# Revit family: Drapery_Track-Lutron-Inside_Curve-Wall_Mount new final
name_source: partatom
category: Specialty Equipment
revit_build: Autodesk Revit 2017 (Build: 20160225_1515(x64)
units: mm (PartAtom-declared; Revit-internal decimal feet)

## family parameters
Cut with Voids When Loaded = Yes
Host = Face
OmniClass Number = 23.30.60.14.21
OmniClass Title = Shades
Part Type = Normal
Room Calculation Point = No
Round Connector Dimension = Use Diameter
Shared = No

## types (3) — shared parameters
Apparent Load = 0 VA
Assembly Code = E2010320
C Radius = 1' - 8"
Default Elevation = 0' - 0"
Description = Inside Curve Wall Mounted Traditional Drapery Track System
Electronic Drive Unit D105 = Yes
Electronic Drive Unit D145 = No
Electronic Drive Unit D175 = No
Electronic Drive Unit Note = Electronic Drive Unit D105 - Carries draperies up to 105 lbs
Finish = Metal - Lutron - White
Instruction Sheet Link = http://www.lutron.com
Load Classification = Motor
Manufacturer = Lutron Electronics Co., Inc
Manufacturer Fax Number = 610-282-1243
Number of Poles = 1
Power Factor = 1
Product Documentation Link = http://www.lutron.com
Product Name = Traditional Drapery Track System
Product Page URL = http://www.lutron.com
Series = Sivoia QS
URL = http://www.lutron.com
Version = 2017 - v1.0a
Voltage = 24 V
Voltage Comment = 24-36V
Warranty URL = http://www.lutron.com
Wattage = 41 W
zero-valued in all types: Cost

## per-type parameters (varying)
| type | C 2nd Drapery | Center Draw | Constraints | Not Tandem | Single Side Draw | Tandem Draw |
| Inside Curve Wall Mounted - Left or Right Side Draw | No | No | 1 | Yes | Yes | No |
| Inside Curve Wall Mounted - Center Draw | Yes | Yes | 2 | Yes | No | No |
| Inside Curve Wall Mounted - Tandem Draw | Yes | No | 3 | No | No | Yes |

note: column(s) folded — value = type name in every type: Model

## geometry (parser evidence)
native form markers: Sweep x10
no freeform markers — native parametric forms only
